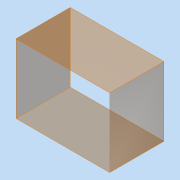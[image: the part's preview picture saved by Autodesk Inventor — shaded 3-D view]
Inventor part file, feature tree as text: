
AUTODESK INVENTOR PART (.ipt)
format: ipt  version: 2013 (Build 170138000, 138)  size: 68,608 bytes
history: native  units: mm
features: sketch x1, other x1, extrude x1
ambient origin geometry x8: Origin, YZ Plane, XZ Plane, XY Plane, X Axis, Y Axis, Z Axis, Center Point
feature tree (3):
  sketch  "Sketch1"  dims[d4=0.0mm]
  other  "Srf1"
  extrude  "ExtrusionSrf1"  [1 undecoded]
note: 1 required parameter value undecoded (feature->parameter linkage not recoverable at this tier; creation-order binding heuristic only, values carry confidence <= 0.55)
